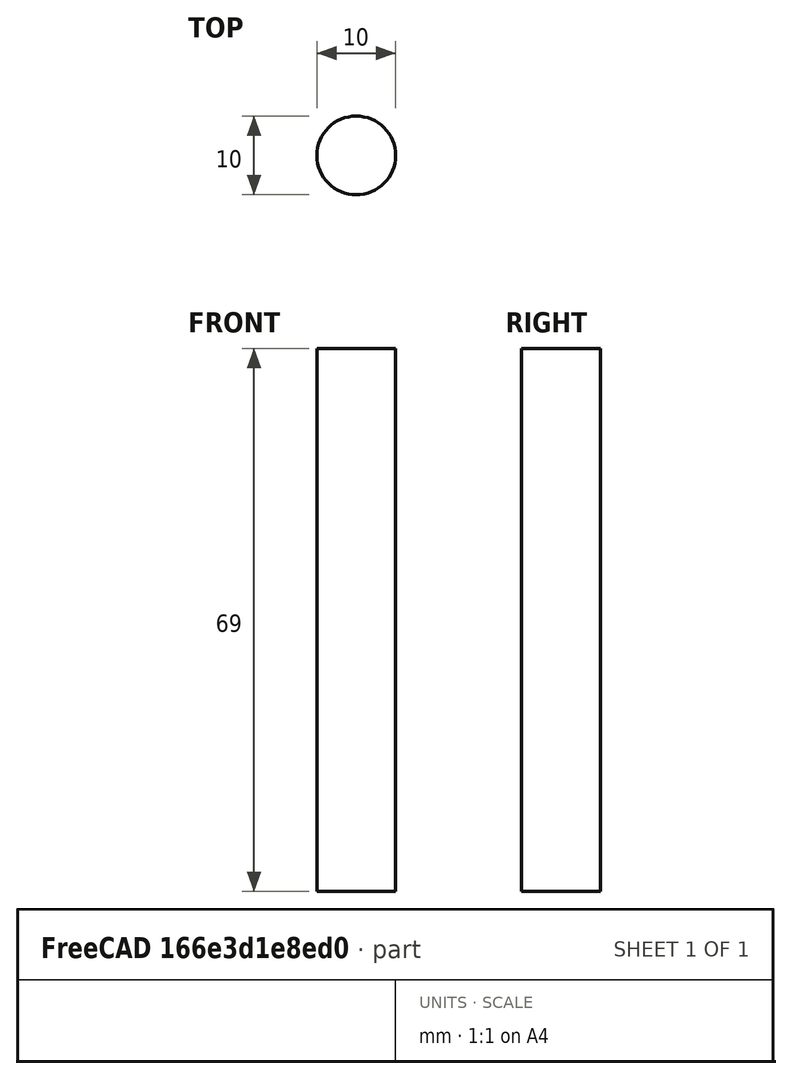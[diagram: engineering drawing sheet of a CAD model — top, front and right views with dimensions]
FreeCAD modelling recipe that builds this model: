
FCSTD DOCUMENT  (FreeCAD 0.19R24267 +99 (Git))
Label: 10mm diameter 69mm long actuator pin FEA_CLEARED
License: All rights reserved
LicenseURL: http://en.wikipedia.org/wiki/All_rights_reserved
objects: PartDesign::Pad×7, Fem::ConstraintForce×2, Sketcher::SketchObject×1, PartDesign::Body×1, Fem::FemSolverObjectPython×1, App::MaterialObjectPython×1, Fem::FemMeshObjectPython×1, Fem::ConstraintFixed×1, Fem::FemAnalysis×1
note: 16 computed .brp shape members not serialized (recipe doc carries the construction recipe); baked Part::Feature solids carry a one-line shape summary decoded from their .brp

FEATURE [Sketcher::SketchObject] Sketch  label="Pin diameter"
  FullyConstrained = true
  MapMode = 5
  Support = -> [XY_Plane]
  sketch-geometry (2):
    g0: ArcOfCircle CenterX=0 CenterY=0 CenterZ=0 NormalX=0 NormalY=0 NormalZ=1 AngleXU=0 Radius=5 StartAngle=4.71239 EndAngle=7.85398
    g1: ArcOfCircle CenterX=0 CenterY=0 CenterZ=0 NormalX=0 NormalY=0 NormalZ=1 AngleXU=0 Radius=5 StartAngle=1.5708 EndAngle=4.71239
  constraints (7):
    c: Coincident(g0,g-1)
    c: PointOnObject(g0,g-2)
    c: PointOnObject(g0,g-2)
    c: Coincident(g1,g0)
    c: Coincident(g1,g0)
    c: Coincident(g1,g0)
    c: Diameter(g0) = 10
FEATURE [PartDesign::Pad] Pad  label="Center gap 10mm"
  Direction = (1,1,1)
  Length = 10
  Length2 = 100
  Profile = -> Sketch
  Reversed = true
  Type = 0
FEATURE [PartDesign::Pad] Pad001  label="Actuator fork 9mm 1"
  BaseFeature = -> Pad
  Direction = (1,1,1)
  Length = 9
  Length2 = 100
  Profile = -> Pad [Face3]
  Type = 0
FEATURE [PartDesign::Pad] Pad002  label="Actuator fork 9mm 2"
  BaseFeature = -> Pad001
  Direction = (1,1,1)
  Length = 9
  Length2 = 100
  Profile = -> Pad001 [Face4]
  Type = 0
FEATURE [PartDesign::Pad] Pad003  label="Lever plate 8mm 1"
  BaseFeature = -> Pad002
  Direction = (1,1,1)
  Length = 8
  Length2 = 100
  Profile = -> Pad002 [Face7]
  Type = 0
FEATURE [PartDesign::Pad] Pad004  label="Lever plate 8mm 2"
  BaseFeature = -> Pad003
  Direction = (1,1,1)
  Length = 8
  Length2 = 100
  Profile = -> Pad003 [Face8]
  Type = 0
FEATURE [PartDesign::Pad] Pad005  label="Free end 12.5mm 1"
  BaseFeature = -> Pad004
  Direction = (1,1,1)
  Length = 12.5
  Length2 = 100
  Profile = -> Pad004 [Face11]
  Type = 0
FEATURE [PartDesign::Pad] Pad006  label="Free end 12.5mm 2"
  BaseFeature = -> Pad005
  Direction = (1,1,1)
  Length = 12.5
  Length2 = 100
  Profile = -> Pad005 [Face12]
  Type = 0
FEATURE [PartDesign::Body] Body
  Group = -> [Sketch,Pad,Pad001,Pad002,Pad003,Pad004,Pad005,Pad006]
  Origin = -> Origin
  Tip = -> Pad006
FEATURE [Fem::FemSolverObjectPython] SolverCcxTools  # FEM object (typed FeaturePython)
  AnalysisType = 0
  BeamShellResultOutput3D = false
  EigenmodeHighLimit = 1000000
  EigenmodeLowLimit = 0
  EigenmodesCount = 10
  GeometricalNonlinearity = 0
  IterationsControlParameterCutb = 0.25,0.5,0.75,0.85,,,1.5,
  IterationsControlParameterIter = 4,8,9,200,10,400,,200,,
  IterationsControlParameterTimeUse = false
  IterationsThermoMechMaximum = 2000
  IterationsUserDefinedIncrementations = false
  IterationsUserDefinedTimeStepLength = false
  MaterialNonlinearity = 0
  MatrixSolverType = 0
  SplitInputWriter = false
  ThermoMechSteadyState = true
  TimeEnd = 1
  TimeInitialStep = 0.01
FEATURE [App::MaterialObjectPython] MaterialSolid  # material (typed FeaturePython)
  Category = 0
  Material = AuthorAndLicense=CalculiX-Steel,CardName=CalculiX-Steel,Density=7900 kg/m^3,Description=Standard steel material for CalculiX sample calculations,+7 more (map truncated)
FEATURE [Fem::FemMeshObjectPython] FEMMeshGmsh  # FEM object (typed FeaturePython)
  Algorithm2D = 0
  Algorithm3D = 0
  CharacteristicLengthMax = 0.8
  CharacteristicLengthMin = 0
  CoherenceMesh = true
  ElementDimension = 0
  ElementOrder = 1
  GeometryTolerance = 1e-06
  GroupsOfNodes = false
  HighOrderOptimize = false
  OptimizeNetgen = false
  OptimizeStd = true
  Part = -> Pad006
  RecombineAll = false
  SecondOrderLinear = false
FEATURE [Fem::ConstraintForce] ConstraintForce  label="Actuator force"
  DirectionVector = (1,-1e-16,0)
  Force = 5000
  NormalDirection = (-1,1e-16,0)
  Points = (18) [(3.06162e-16,5,9),(-5,6.12323e-16,9),(-9.18485e-16,-5,9),(3.06162e-16,5,4.5),(-5,6.12323e-16,4.5),(-9.18485e-16,-5,4.5),(3.06162e-16,5,0),+11 more]
  References = -> [Pad006]
  Reversed = true
FEATURE [Fem::ConstraintForce] ConstraintForce001  label="Lever arm force"
  DirectionVector = (-1,2e-16,0)
  Force = 5000
  NormalDirection = (1,-2e-16,0)
  Points = (18) [(-9.18485e-16,-5,-27),(5,-1.22465e-15,-27),(1.53081e-15,5,-27),(-9.18485e-16,-5,-23),(5,-1.22465e-15,-23),(1.53081e-15,5,-23),(-9.18485e-16,-5,-19),+11 more]
  References = -> [Pad006]
  Reversed = true
FEATURE [Fem::ConstraintFixed] ConstraintFixed
  NormalDirection = (0,0,1)
  Normals = (2) [(0,0,1),(0,0,1)]
  Points = (2) [(-9.18485e-16,-5,-39.5),(1.53081e-15,5,-39.5)]
  References = -> [Pad006]
FEATURE [Fem::FemAnalysis] Analysis
  Group = -> [SolverCcxTools,MaterialSolid,FEMMeshGmsh,ConstraintForce,ConstraintForce001,ConstraintFixed]
